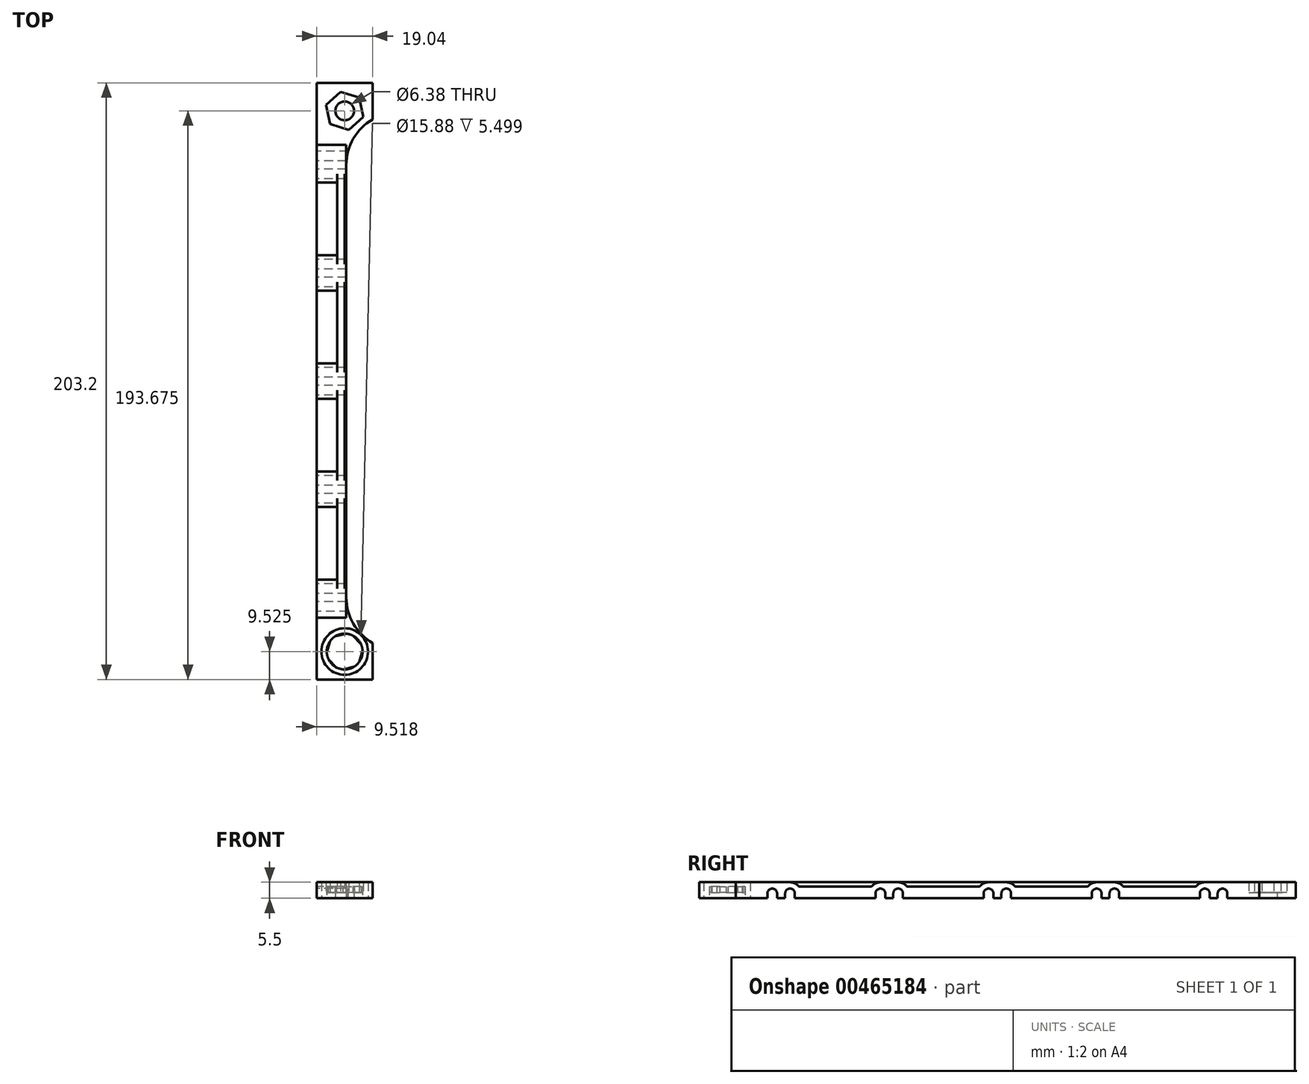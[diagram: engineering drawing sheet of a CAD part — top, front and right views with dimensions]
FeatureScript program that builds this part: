
annotation { "Feature Type Name" : "Feature", "Feature Type Description" : "" }
export const myFeature = defineFeature(function(context is Context, id is Id, definition is map)
    precondition{}
    {
        {
            var Q0;
            Q0=qCreatedBy(makeId("Top.planeOp"),FACE);
            var sketch = newSketch(context, id + "F0", { "sketchPlane" : qUnion([Q0])});
            skLineSegment(sketch, "E0.bottom", {"start": v(-101.58, -101.6) * mm, "end": v(-82.54, -101.6) * mm});
            skLineSegment(sketch, "E0.top", {"start": v(-101.58, 101.6) * mm, "end": v(-82.54, 101.6) * mm});
            skLineSegment(sketch, "E0.left", {"start": v(-101.58, -101.6) * mm, "end": v(-101.58, 101.6) * mm});
            skLineSegment(sketch, "E1.right", {"start": v(-92.06, -92.08) * mm, "end": v(-92.06, 92.08) * mm, "construction": true});
            skCircle(sketch, "E2.2.1.1", {"center": v(-73.66, -73.66) * mm, "radius": 17.85 * mm});
            skCircle(sketch, "E3.0.1.1", {"center": v(-73.66, -36.83) * mm, "radius": 17.85 * mm});
            skCircle(sketch, "E3.0.2.1", {"center": v(-73.66, 0) * mm, "radius": 17.85 * mm});
            skCircle(sketch, "E3.0.3.1", {"center": v(-73.66, 36.83) * mm, "radius": 17.85 * mm});
            skCircle(sketch, "E3.0.4.1", {"center": v(-73.66, 73.66) * mm, "radius": 17.85 * mm});
            skLineSegment(sketch, "E4.left", {"start": v(-94.6, 94.61) * mm, "end": v(-94.6, -94.62) * mm, "construction": true});
            skCircle(sketch, "E5", {"center": v(-92.06, 92.07) * mm, "radius": 6.1 * mm});
            skCircle(sketch, "E6", {"center": v(-92.06, 92.07) * mm, "radius": 3.19 * mm});
            skCircle(sketch, "E7.MirrorC", {"center": v(-92.06, -92.07) * mm, "radius": 3.19 * mm});
            skCircle(sketch, "E8.MirrorC", {"center": v(-92.06, -92.07) * mm, "radius": 6.1 * mm});
            skCircle(sketch, "E9", {"center": v(-92.06, 92.07) * mm, "radius": 7.94 * mm});
            skCircle(sketch, "E10.MirrorC", {"center": v(-92.06, -92.07) * mm, "radius": 7.94 * mm});
            skCircle(sketch, "E11", {"center": v(-73.65, -73.66) * mm, "radius": 16.38 * mm});
            skCircle(sketch, "E12.0.1.0", {"center": v(-73.65, -36.83) * mm, "radius": 16.38 * mm});
            skCircle(sketch, "E12.0.2.0", {"center": v(-73.65, 0) * mm, "radius": 16.38 * mm});
            skCircle(sketch, "E12.0.3.0", {"center": v(-73.65, 36.83) * mm, "radius": 16.38 * mm});
            skCircle(sketch, "E12.0.4.0", {"center": v(-73.65, 73.66) * mm, "radius": 16.38 * mm});
            skLineSegment(sketch, "E13.right", {"start": v(-101.58, -81.01) * mm, "end": v(-101.58, -68.33) * mm});
            skLineSegment(sketch, "E14.0.1.2", {"start": v(-101.6, -6.34) * mm, "end": v(-101.6, 6.34) * mm});
            skLineSegment(sketch, "E14.0.2.2", {"start": v(-101.62, 68.33) * mm, "end": v(-101.62, 81.01) * mm});
            skLineSegment(sketch, "E14.direction2", {"start": v(-101.58, -81.01) * mm, "end": v(-101.6, -6.34) * mm, "construction": true});
            skLineSegment(sketch, "E15", {"start": v(-101.58, 0) * mm, "end": v(-73.65, 0) * mm, "construction": true});
            skLineSegment(sketch, "E16", {"start": v(-82.54, 101.6) * mm, "end": v(-82.54, -101.6) * mm});
            skLineSegment(sketch, "E17", {"start": v(-92.06, -92.08) * mm, "end": v(-92.06, -101.6) * mm});
            skLineSegment(sketch, "E18", {"start": v(-73.65, 73.66) * mm, "end": v(-101.62, 73.66) * mm, "construction": true});
            skLineSegment(sketch, "E19", {"start": v(-73.65, 36.83) * mm, "end": v(-101.58, 36.83) * mm, "construction": true});
            skLineSegment(sketch, "E20", {"start": v(-73.65, -36.83) * mm, "end": v(-101.58, -36.83) * mm, "construction": true});
            skLineSegment(sketch, "E21", {"start": v(-73.65, -73.66) * mm, "end": v(-101.58, -73.66) * mm, "construction": true});
            skLineSegment(sketch, "E22", {"start": v(-91.5, 73.66) * mm, "end": v(-91.5, -73.66) * mm});
            skLineSegment(sketch, "E23.bottom", {"start": v(-94.6, -73.66) * mm, "end": v(-92.06, -73.66) * mm});
            skLineSegment(sketch, "E23.top", {"start": v(-94.6, 73.66) * mm, "end": v(-92.06, 73.66) * mm});
            skLineSegment(sketch, "E23.left", {"start": v(-94.6, -73.66) * mm, "end": v(-94.6, 73.66) * mm});
            skLineSegment(sketch, "E23.right", {"start": v(-92.06, -73.66) * mm, "end": v(-92.06, 73.66) * mm});
            skSolve(sketch);
        }
        {
            var Q0;
            {var subQ9=sQuery(id+"F0.wireOp",EDGE,"E0.top");Q0=makeQuery(id+"F0.imprint","IMPRINT",FACE,{"disambiguationData":[TD([[makeQuery(id+"F0.imprint","IMPRINT",EDGE,{"derivedFrom":subQ9}),-1.0]])]});}
            var Q1;
            Q1=makeQuery(id+"F0.imprint","IMPRINT",FACE,{"disambiguationData":[TD([[makeQuery(id+"F0.imprint","IMPRINT",EDGE,{"derivedFrom":sQuery(id+"F0.wireOp",EDGE,"E5")}),-1.0]])]});
            var Q2;
            Q2=makeQuery(id+"F0.imprint","IMPRINT",FACE,{"disambiguationData":[TD([[makeQuery(id+"F0.imprint","IMPRINT",EDGE,{"derivedFrom":sQuery(id+"F0.wireOp",EDGE,"E5")}),1.0]])]});
            var Q3;
            Q3=makeQuery(id+"F0.imprint","IMPRINT",FACE,{"disambiguationData":[TD([[makeQuery(id+"F0.imprint","IMPRINT",EDGE,{"derivedFrom":sQuery(id+"F0.wireOp",EDGE,"E8.MirrorC")}),1.0]])]});
            var Q4;
            Q4=makeQuery(id+"F0.imprint","IMPRINT",FACE,{"disambiguationData":[TD([[makeQuery(id+"F0.imprint","IMPRINT",EDGE,{"derivedFrom":sQuery(id+"F0.wireOp",EDGE,"E7.MirrorC")}),1.0]])]});
            extrude(context, id + "F1", {"entities" : qUnion([Q0, Q1, Q2, Q3, Q4]), "depth" : 4 * mm, "offsetDistance" : 25.4 * mm});
        }
        {
            var Q0;
            Q0=makeQuery(id+"F1.opExtrude","SWEPT_FACE",FACE,{"disambiguationData":[OSD([sQuery(id+"F0.wireOp",EDGE,"E0.left"),sQuery(id+"F0.wireOp",EDGE,"E13.right")])]});
            cPlane(context, id + "F2", {"entities" : qUnion([Q0]), "cplaneType" : CPlaneType.OFFSET, "offset" : 0 * mm, "width" : 152.4 * mm, "height" : 152.4 * mm});
        }
        {
            var Q0;
            Q0=qCreatedBy(id+"F2.planeOp",FACE);
            var sketch = newSketch(context, id + "F3", { "sketchPlane" : qUnion([Q0])});
            skLineSegment(sketch, "E24.bottom", {"start": v(-75.03, 0) * mm, "end": v(-78.33, 0) * mm});
            skLineSegment(sketch, "E24.top", {"start": v(-75.03, 1.65) * mm, "end": v(-78.33, 1.65) * mm});
            skLineSegment(sketch, "E24.left", {"start": v(-75.03, 0) * mm, "end": v(-75.03, 1.65) * mm});
            skLineSegment(sketch, "E24.right", {"start": v(-78.33, 0) * mm, "end": v(-78.33, 1.65) * mm});
            skLineSegment(sketch, "E25.bottom", {"start": v(-72.29, 0) * mm, "end": v(-68.99, 0) * mm});
            skLineSegment(sketch, "E25.top", {"start": v(-72.29, 1.65) * mm, "end": v(-68.99, 1.65) * mm});
            skLineSegment(sketch, "E25.left", {"start": v(-72.29, 0) * mm, "end": v(-72.29, 1.65) * mm});
            skLineSegment(sketch, "E25.right", {"start": v(-68.99, 0) * mm, "end": v(-68.99, 1.65) * mm});
            skArc(sketch, "E26", {"start": v(-75.03, 1.65) * mm, "mid": v(-76.68, 3.3) * mm, "end": v(-78.33, 1.65) * mm});
            skArc(sketch, "E27", {"start": v(-68.99, 1.65) * mm, "mid": v(-70.64, 3.3) * mm, "end": v(-72.29, 1.65) * mm});
            skArc(sketch, "E28", {"start": v(-70.64, 5.46) * mm, "mid": v(-67.94, 4.34) * mm, "end": v(-66.83, 1.65) * mm});
            skPoint(sketch, "E28.startSnap0", {"position": v(-70.64, 3.3) * mm});
            skLineSegment(sketch, "E29", {"start": v(-76.68, 5.46) * mm, "end": v(-70.64, 5.46) * mm});
            skLineSegment(sketch, "E30", {"start": v(-80.5, 1.65) * mm, "end": v(-78.33, 1.65) * mm});
            skLineSegment(sketch, "E31", {"start": v(-75.03, 1.65) * mm, "end": v(-72.29, 1.65) * mm});
            skLineSegment(sketch, "E32", {"start": v(-68.99, 1.65) * mm, "end": v(-66.83, 1.65) * mm});
            skLineSegment(sketch, "E33", {"start": v(-76.68, 1.65) * mm, "end": v(-76.68, 0) * mm, "construction": true});
            skLineSegment(sketch, "E34", {"start": v(-70.64, 1.65) * mm, "end": v(-70.64, 0) * mm, "construction": true});
            skLineSegment(sketch, "E35.bottom", {"start": v(-38.2, 0) * mm, "end": v(-41.5, 0) * mm});
            skLineSegment(sketch, "E35.top", {"start": v(-38.2, 1.65) * mm, "end": v(-41.5, 1.65) * mm});
            skLineSegment(sketch, "E35.left", {"start": v(-38.2, 0) * mm, "end": v(-38.2, 1.65) * mm});
            skLineSegment(sketch, "E35.right", {"start": v(-41.5, 0) * mm, "end": v(-41.5, 1.65) * mm});
            skLineSegment(sketch, "E36.bottom", {"start": v(-35.46, 0) * mm, "end": v(-32.16, 0) * mm});
            skLineSegment(sketch, "E36.top", {"start": v(-35.46, 1.65) * mm, "end": v(-32.16, 1.65) * mm});
            skLineSegment(sketch, "E36.left", {"start": v(-35.46, 0) * mm, "end": v(-35.46, 1.65) * mm});
            skLineSegment(sketch, "E36.right", {"start": v(-32.16, 0) * mm, "end": v(-32.16, 1.65) * mm});
            skArc(sketch, "E37", {"start": v(-38.2, 1.65) * mm, "mid": v(-39.85, 3.3) * mm, "end": v(-41.5, 1.65) * mm});
            skArc(sketch, "E38", {"start": v(-32.16, 1.65) * mm, "mid": v(-33.8, 3.3) * mm, "end": v(-35.46, 1.65) * mm});
            skArc(sketch, "E39", {"start": v(-43.66, 1.65) * mm, "mid": v(-42.55, 4.34) * mm, "end": v(-39.85, 5.46) * mm});
            skArc(sketch, "E40", {"start": v(-33.8, 5.46) * mm, "mid": v(-31.11, 4.34) * mm, "end": v(-30, 1.65) * mm});
            skPoint(sketch, "E40.startSnap0", {"position": v(-33.8, 3.3) * mm});
            skLineSegment(sketch, "E41", {"start": v(-39.85, 5.46) * mm, "end": v(-33.8, 5.46) * mm});
            skLineSegment(sketch, "E42", {"start": v(-43.66, 1.65) * mm, "end": v(-41.5, 1.65) * mm});
            skLineSegment(sketch, "E43", {"start": v(-38.2, 1.65) * mm, "end": v(-35.46, 1.65) * mm});
            skLineSegment(sketch, "E44", {"start": v(-32.16, 1.65) * mm, "end": v(-30, 1.65) * mm});
            skLineSegment(sketch, "E45", {"start": v(-39.85, 1.65) * mm, "end": v(-39.85, 0) * mm, "construction": true});
            skLineSegment(sketch, "E46", {"start": v(-33.8, 1.65) * mm, "end": v(-33.8, 0) * mm, "construction": true});
            skLineSegment(sketch, "E47.bottom", {"start": v(-1.37, 0) * mm, "end": v(-4.67, 0) * mm});
            skLineSegment(sketch, "E47.top", {"start": v(-1.37, 1.65) * mm, "end": v(-4.67, 1.65) * mm});
            skLineSegment(sketch, "E47.left", {"start": v(-1.37, 0) * mm, "end": v(-1.37, 1.65) * mm});
            skLineSegment(sketch, "E47.right", {"start": v(-4.67, 0) * mm, "end": v(-4.67, 1.65) * mm});
            skLineSegment(sketch, "E48.bottom", {"start": v(1.37, 0) * mm, "end": v(4.67, 0) * mm});
            skLineSegment(sketch, "E48.top", {"start": v(1.37, 1.65) * mm, "end": v(4.67, 1.65) * mm});
            skLineSegment(sketch, "E48.left", {"start": v(1.37, 0) * mm, "end": v(1.37, 1.65) * mm});
            skLineSegment(sketch, "E48.right", {"start": v(4.67, 0) * mm, "end": v(4.67, 1.65) * mm});
            skArc(sketch, "E49", {"start": v(-1.37, 1.65) * mm, "mid": v(-3.02, 3.3) * mm, "end": v(-4.67, 1.65) * mm});
            skArc(sketch, "E50", {"start": v(4.67, 1.65) * mm, "mid": v(3.02, 3.3) * mm, "end": v(1.37, 1.65) * mm});
            skArc(sketch, "E51", {"start": v(-6.83, 1.65) * mm, "mid": v(-5.72, 4.34) * mm, "end": v(-3.02, 5.46) * mm});
            skArc(sketch, "E52", {"start": v(3.02, 5.46) * mm, "mid": v(5.72, 4.34) * mm, "end": v(6.83, 1.65) * mm});
            skPoint(sketch, "E52.startSnap0", {"position": v(3.02, 3.3) * mm});
            skLineSegment(sketch, "E53", {"start": v(-3.02, 5.46) * mm, "end": v(3.02, 5.46) * mm});
            skLineSegment(sketch, "E54", {"start": v(-6.83, 1.65) * mm, "end": v(-4.67, 1.65) * mm});
            skLineSegment(sketch, "E55", {"start": v(-1.37, 1.65) * mm, "end": v(1.37, 1.65) * mm});
            skLineSegment(sketch, "E56", {"start": v(4.67, 1.65) * mm, "end": v(6.83, 1.65) * mm});
            skLineSegment(sketch, "E57", {"start": v(-3.02, 1.65) * mm, "end": v(-3.02, 0) * mm, "construction": true});
            skLineSegment(sketch, "E58", {"start": v(3.02, 1.65) * mm, "end": v(3.02, 0) * mm, "construction": true});
            skLineSegment(sketch, "E59.bottom", {"start": v(35.46, 0) * mm, "end": v(32.16, 0) * mm});
            skLineSegment(sketch, "E59.top", {"start": v(35.46, 1.65) * mm, "end": v(32.16, 1.65) * mm});
            skLineSegment(sketch, "E59.left", {"start": v(35.46, 0) * mm, "end": v(35.46, 1.65) * mm});
            skLineSegment(sketch, "E59.right", {"start": v(32.16, 0) * mm, "end": v(32.16, 1.65) * mm});
            skLineSegment(sketch, "E60.bottom", {"start": v(38.2, 0) * mm, "end": v(41.5, 0) * mm});
            skLineSegment(sketch, "E60.top", {"start": v(38.2, 1.65) * mm, "end": v(41.5, 1.65) * mm});
            skLineSegment(sketch, "E60.left", {"start": v(38.2, 0) * mm, "end": v(38.2, 1.65) * mm});
            skLineSegment(sketch, "E60.right", {"start": v(41.5, 0) * mm, "end": v(41.5, 1.65) * mm});
            skArc(sketch, "E61", {"start": v(35.46, 1.65) * mm, "mid": v(33.8, 3.3) * mm, "end": v(32.16, 1.65) * mm});
            skArc(sketch, "E62", {"start": v(41.5, 1.65) * mm, "mid": v(39.85, 3.3) * mm, "end": v(38.2, 1.65) * mm});
            skArc(sketch, "E63", {"start": v(30, 1.65) * mm, "mid": v(31.11, 4.34) * mm, "end": v(33.8, 5.46) * mm});
            skArc(sketch, "E64", {"start": v(39.85, 5.46) * mm, "mid": v(42.55, 4.34) * mm, "end": v(43.66, 1.65) * mm});
            skPoint(sketch, "E64.startSnap0", {"position": v(39.85, 3.3) * mm});
            skLineSegment(sketch, "E65", {"start": v(33.8, 5.46) * mm, "end": v(39.85, 5.46) * mm});
            skLineSegment(sketch, "E66", {"start": v(30, 1.65) * mm, "end": v(32.16, 1.65) * mm});
            skLineSegment(sketch, "E67", {"start": v(35.46, 1.65) * mm, "end": v(38.2, 1.65) * mm});
            skLineSegment(sketch, "E68", {"start": v(41.5, 1.65) * mm, "end": v(43.66, 1.65) * mm});
            skLineSegment(sketch, "E69", {"start": v(33.8, 1.65) * mm, "end": v(33.8, 0) * mm, "construction": true});
            skLineSegment(sketch, "E70", {"start": v(39.85, 1.65) * mm, "end": v(39.85, 0) * mm, "construction": true});
            skLineSegment(sketch, "E71.bottom", {"start": v(72.29, 0) * mm, "end": v(68.99, 0) * mm});
            skLineSegment(sketch, "E71.top", {"start": v(72.29, 1.65) * mm, "end": v(68.99, 1.65) * mm});
            skLineSegment(sketch, "E71.left", {"start": v(72.29, 0) * mm, "end": v(72.29, 1.65) * mm});
            skLineSegment(sketch, "E71.right", {"start": v(68.99, 0) * mm, "end": v(68.99, 1.65) * mm});
            skLineSegment(sketch, "E72.bottom", {"start": v(75.03, 0) * mm, "end": v(78.33, 0) * mm});
            skLineSegment(sketch, "E72.top", {"start": v(75.03, 1.65) * mm, "end": v(78.33, 1.65) * mm});
            skLineSegment(sketch, "E72.left", {"start": v(75.03, 0) * mm, "end": v(75.03, 1.65) * mm});
            skLineSegment(sketch, "E72.right", {"start": v(78.33, 0) * mm, "end": v(78.33, 1.65) * mm});
            skArc(sketch, "E73", {"start": v(72.29, 1.65) * mm, "mid": v(70.64, 3.3) * mm, "end": v(68.99, 1.65) * mm});
            skArc(sketch, "E74", {"start": v(78.33, 1.65) * mm, "mid": v(76.68, 3.3) * mm, "end": v(75.03, 1.65) * mm});
            skArc(sketch, "E75", {"start": v(66.83, 1.65) * mm, "mid": v(67.94, 4.34) * mm, "end": v(70.64, 5.46) * mm});
            skPoint(sketch, "E76.startSnap0", {"position": v(76.68, 3.3) * mm});
            skLineSegment(sketch, "E77", {"start": v(70.64, 5.46) * mm, "end": v(76.68, 5.46) * mm});
            skLineSegment(sketch, "E78", {"start": v(66.83, 1.65) * mm, "end": v(68.99, 1.65) * mm});
            skLineSegment(sketch, "E79", {"start": v(72.29, 1.65) * mm, "end": v(75.03, 1.65) * mm});
            skLineSegment(sketch, "E80", {"start": v(78.33, 1.65) * mm, "end": v(80.5, 1.65) * mm});
            skLineSegment(sketch, "E81", {"start": v(70.64, 1.65) * mm, "end": v(70.64, 0) * mm, "construction": true});
            skLineSegment(sketch, "E82", {"start": v(76.68, 1.65) * mm, "end": v(76.68, 0) * mm, "construction": true});
            skLineSegment(sketch, "E83", {"start": v(80.5, 1.65) * mm, "end": v(80.5, 5.46) * mm});
            skLineSegment(sketch, "E84", {"start": v(80.5, 5.46) * mm, "end": v(76.68, 5.46) * mm});
            skLineSegment(sketch, "E85", {"start": v(-80.5, 1.65) * mm, "end": v(-80.5, 5.46) * mm});
            skLineSegment(sketch, "E86", {"start": v(-80.5, 5.46) * mm, "end": v(-76.68, 5.46) * mm});
            skSolve(sketch);
        }
        {
            var Q0;
            Q0=makeQuery(id+"F0.imprint","IMPRINT",FACE,{"disambiguationData":[TD([[makeQuery(id+"F0.imprint","IMPRINT",EDGE,{"derivedFrom":sQuery(id+"F0.wireOp",EDGE,"E23.bottom")}),1.0]])]});
            extrude(context, id + "F4", {"entities" : qUnion([Q0]), "operationType" : NewBodyOperationType.ADD, "depth" : 5.46 * mm, "offsetDistance" : 25.4 * mm});
        }
        {
            var Q0;
            Q0=makeQuery(id+"F3.imprint","IMPRINT",FACE,{"disambiguationData":[TD([[makeQuery(id+"F3.imprint","IMPRINT",EDGE,{"derivedFrom":sQuery(id+"F3.wireOp",EDGE,"E26")}),-1.0]])]});
            var Q1;
            Q1=makeQuery(id+"F3.imprint","IMPRINT",FACE,{"disambiguationData":[TD([[makeQuery(id+"F3.imprint","IMPRINT",EDGE,{"derivedFrom":sQuery(id+"F3.wireOp",EDGE,"E37")}),-1.0]])]});
            var Q2;
            Q2=makeQuery(id+"F3.imprint","IMPRINT",FACE,{"disambiguationData":[TD([[makeQuery(id+"F3.imprint","IMPRINT",EDGE,{"derivedFrom":sQuery(id+"F3.wireOp",EDGE,"E49")}),-1.0]])]});
            var Q3;
            Q3=makeQuery(id+"F3.imprint","IMPRINT",FACE,{"disambiguationData":[TD([[makeQuery(id+"F3.imprint","IMPRINT",EDGE,{"derivedFrom":sQuery(id+"F3.wireOp",EDGE,"E61")}),-1.0]])]});
            var Q4;
            Q4=makeQuery(id+"F3.imprint","IMPRINT",FACE,{"disambiguationData":[TD([[makeQuery(id+"F3.imprint","IMPRINT",EDGE,{"derivedFrom":sQuery(id+"F3.wireOp",EDGE,"E73")}),-1.0]])]});
            var Q5;
            Q5=makeQuery(id+"F1.opExtrude","SWEPT_FACE",FACE,{"disambiguationData":[OSD([sQuery(id+"F0.wireOp",EDGE,"E22")])]});
            extrude(context, id + "F5", {"entities" : qUnion([Q0, Q1, Q2, Q3, Q4]), "operationType" : NewBodyOperationType.ADD, "endBound" : BoundingType.UP_TO_SURFACE, "oppositeDirection" : true, "depth" : 25.4 * mm, "endBoundEntityFace" : qUnion([Q5]), "offsetDistance" : 25.4 * mm});
        }
        {
            var Q0;
            Q0=makeQuery(id+"F3.imprint","IMPRINT",FACE,{"disambiguationData":[TD([[makeQuery(id+"F3.imprint","IMPRINT",EDGE,{"derivedFrom":sQuery(id+"F3.wireOp",EDGE,"E24.bottom")}),-1.0]])]});
            var Q1;
            Q1=makeQuery(id+"F3.imprint","IMPRINT",FACE,{"disambiguationData":[TD([[makeQuery(id+"F3.imprint","IMPRINT",EDGE,{"derivedFrom":sQuery(id+"F3.wireOp",EDGE,"E25.bottom")}),1.0]])]});
            var Q2;
            Q2=makeQuery(id+"F3.imprint","IMPRINT",FACE,{"disambiguationData":[TD([[makeQuery(id+"F3.imprint","IMPRINT",EDGE,{"derivedFrom":sQuery(id+"F3.wireOp",EDGE,"E25.top")}),1.0]])]});
            var Q3;
            Q3=makeQuery(id+"F3.imprint","IMPRINT",FACE,{"disambiguationData":[TD([[makeQuery(id+"F3.imprint","IMPRINT",EDGE,{"derivedFrom":sQuery(id+"F3.wireOp",EDGE,"E24.top")}),-1.0]])]});
            var Q4;
            Q4=makeQuery(id+"F3.imprint","IMPRINT",FACE,{"disambiguationData":[TD([[makeQuery(id+"F3.imprint","IMPRINT",EDGE,{"derivedFrom":sQuery(id+"F3.wireOp",EDGE,"E35.top")}),-1.0]])]});
            var Q5;
            Q5=makeQuery(id+"F3.imprint","IMPRINT",FACE,{"disambiguationData":[TD([[makeQuery(id+"F3.imprint","IMPRINT",EDGE,{"derivedFrom":sQuery(id+"F3.wireOp",EDGE,"E36.top")}),1.0]])]});
            var Q6;
            Q6=makeQuery(id+"F3.imprint","IMPRINT",FACE,{"disambiguationData":[TD([[makeQuery(id+"F3.imprint","IMPRINT",EDGE,{"derivedFrom":sQuery(id+"F3.wireOp",EDGE,"E36.bottom")}),1.0]])]});
            var Q7;
            Q7=makeQuery(id+"F3.imprint","IMPRINT",FACE,{"disambiguationData":[TD([[makeQuery(id+"F3.imprint","IMPRINT",EDGE,{"derivedFrom":sQuery(id+"F3.wireOp",EDGE,"E35.bottom")}),-1.0]])]});
            var Q8;
            Q8=makeQuery(id+"F3.imprint","IMPRINT",FACE,{"disambiguationData":[TD([[makeQuery(id+"F3.imprint","IMPRINT",EDGE,{"derivedFrom":sQuery(id+"F3.wireOp",EDGE,"E47.top")}),-1.0]])]});
            var Q9;
            Q9=makeQuery(id+"F3.imprint","IMPRINT",FACE,{"disambiguationData":[TD([[makeQuery(id+"F3.imprint","IMPRINT",EDGE,{"derivedFrom":sQuery(id+"F3.wireOp",EDGE,"E47.bottom")}),-1.0]])]});
            var Q10;
            Q10=makeQuery(id+"F3.imprint","IMPRINT",FACE,{"disambiguationData":[TD([[makeQuery(id+"F3.imprint","IMPRINT",EDGE,{"derivedFrom":sQuery(id+"F3.wireOp",EDGE,"E48.top")}),1.0]])]});
            var Q11;
            Q11=makeQuery(id+"F3.imprint","IMPRINT",FACE,{"disambiguationData":[TD([[makeQuery(id+"F3.imprint","IMPRINT",EDGE,{"derivedFrom":sQuery(id+"F3.wireOp",EDGE,"E48.bottom")}),1.0]])]});
            var Q12;
            Q12=makeQuery(id+"F3.imprint","IMPRINT",FACE,{"disambiguationData":[TD([[makeQuery(id+"F3.imprint","IMPRINT",EDGE,{"derivedFrom":sQuery(id+"F3.wireOp",EDGE,"E59.bottom")}),-1.0]])]});
            var Q13;
            Q13=makeQuery(id+"F3.imprint","IMPRINT",FACE,{"disambiguationData":[TD([[makeQuery(id+"F3.imprint","IMPRINT",EDGE,{"derivedFrom":sQuery(id+"F3.wireOp",EDGE,"E59.top")}),-1.0]])]});
            var Q14;
            Q14=makeQuery(id+"F3.imprint","IMPRINT",FACE,{"disambiguationData":[TD([[makeQuery(id+"F3.imprint","IMPRINT",EDGE,{"derivedFrom":sQuery(id+"F3.wireOp",EDGE,"E60.bottom")}),1.0]])]});
            var Q15;
            Q15=makeQuery(id+"F3.imprint","IMPRINT",FACE,{"disambiguationData":[TD([[makeQuery(id+"F3.imprint","IMPRINT",EDGE,{"derivedFrom":sQuery(id+"F3.wireOp",EDGE,"E60.top")}),1.0]])]});
            var Q16;
            Q16=makeQuery(id+"F3.imprint","IMPRINT",FACE,{"disambiguationData":[TD([[makeQuery(id+"F3.imprint","IMPRINT",EDGE,{"derivedFrom":sQuery(id+"F3.wireOp",EDGE,"E71.bottom")}),-1.0]])]});
            var Q17;
            Q17=makeQuery(id+"F3.imprint","IMPRINT",FACE,{"disambiguationData":[TD([[makeQuery(id+"F3.imprint","IMPRINT",EDGE,{"derivedFrom":sQuery(id+"F3.wireOp",EDGE,"E71.top")}),-1.0]])]});
            var Q18;
            Q18=makeQuery(id+"F3.imprint","IMPRINT",FACE,{"disambiguationData":[TD([[makeQuery(id+"F3.imprint","IMPRINT",EDGE,{"derivedFrom":sQuery(id+"F3.wireOp",EDGE,"E72.top")}),1.0]])]});
            var Q19;
            Q19=makeQuery(id+"F3.imprint","IMPRINT",FACE,{"disambiguationData":[TD([[makeQuery(id+"F3.imprint","IMPRINT",EDGE,{"derivedFrom":sQuery(id+"F3.wireOp",EDGE,"E72.bottom")}),1.0]])]});
            var Q20;
            Q20=makeQuery(id+"F1.opExtrude","SWEPT_BODY",BODY,{"disambiguationData":[OSD([sQuery(id+"F0.wireOp",EDGE,"E0.bottom"),sQuery(id+"F0.wireOp",EDGE,"E0.top"),sQuery(id+"F0.wireOp",EDGE,"E0.left"),sQuery(id+"F0.wireOp",EDGE,"E2.2.1.1"),sQuery(id+"F0.wireOp",EDGE,"E3.0.4.1"),sQuery(id+"F0.wireOp",EDGE,"E6"),sQuery(id+"F0.wireOp",EDGE,"E7.MirrorC"),sQuery(id+"F0.wireOp",EDGE,"E13.right"),sQuery(id+"F0.wireOp",EDGE,"E16"),sQuery(id+"F0.wireOp",EDGE,"E22")])]});
            extrude(context, id + "F6", {"entities" : qUnion([Q0, Q1, Q2, Q3, Q4, Q5, Q6, Q7, Q8, Q9, Q10, Q11, Q12, Q13, Q14, Q15, Q16, Q17, Q18, Q19]), "operationType" : NewBodyOperationType.REMOVE, "endBound" : BoundingType.THROUGH_ALL, "oppositeDirection" : true, "depth" : 25.4 * mm, "endBoundEntityBody" : qUnion([Q20]), "offsetDistance" : 25.4 * mm});
        }
        {
            var Q0;
            {var subQ0=sQuery(id+"F0.wireOp",EDGE,"E13.right");var subQ1=sQuery(id+"F0.wireOp",EDGE,"E0.left");var subQ2=sQuery(id+"F3.wireOp",EDGE,"f0gCdHVo-Gz2e-MZJZ-KHlR-wAMuaOjWp0eY");var subQ3=sQuery(id+"F0.wireOp",EDGE,"E22");var subQ4=sQuery(id+"F0.wireOp",EDGE,"E16");var subQ5=sQuery(id+"F0.wireOp",EDGE,"E0.top");var subQ6=sQuery(id+"F0.wireOp",EDGE,"E3.0.4.1");var subQ7=sQuery(id+"F0.wireOp",EDGE,"E6");Q0=makeQuery(id+"F5.boolean.opBoolean","SPLIT",FACE,{"disambiguationData":[TD([makeQuery(id+"F1.opExtrude","SWEPT_FACE",FACE,{"disambiguationData":[OSD([subQ5])]}),makeQuery(id+"F1.opExtrude","SWEPT_FACE",FACE,{"disambiguationData":[OSD([subQ1,subQ0])]}),makeQuery(id+"F1.opExtrude","SWEPT_FACE",FACE,{"disambiguationData":[OSD([subQ6])]}),makeQuery(id+"F1.opExtrude","SWEPT_FACE",FACE,{"disambiguationData":[OSD([subQ7])]}),makeQuery(id+"F1.opExtrude","SWEPT_FACE",FACE,{"disambiguationData":[OSD([subQ4]),TDD([makeQuery(id+"F0.imprint","IMPRINT",EDGE,{"disambiguationData":[TD([[makeQuery(id+"F0.imprint","INTERSECT",VERTEX,{"derivedFrom":[subQ5,subQ4]}),-1.0]])],"derivedFrom":subQ4})])]}),makeQuery(id+"F1.opExtrude","SWEPT_FACE",FACE,{"disambiguationData":[OSD([subQ3])]}),makeQuery(id+"F5.opExtrude","CAP_FACE",FACE,{"disambiguationData":[OSD([sQuery(id+"F3.wireOp",EDGE,"E26"),sQuery(id+"F3.wireOp",EDGE,"E27"),subQ2,sQuery(id+"F3.wireOp",EDGE,"E28"),sQuery(id+"F3.wireOp",EDGE,"E29"),sQuery(id+"F3.wireOp",EDGE,"E30"),sQuery(id+"F3.wireOp",EDGE,"E31"),sQuery(id+"F3.wireOp",EDGE,"E32")])],"isStart":true}),makeQuery(id+"F5.opExtrude","SWEPT_FACE",FACE,{"disambiguationData":[OSD([subQ2])]}),makeQuery(id+"F5.opExtrude","CAP_FACE",FACE,{"disambiguationData":[OSD([sQuery(id+"F3.wireOp",EDGE,"E37"),sQuery(id+"F3.wireOp",EDGE,"E38"),sQuery(id+"F3.wireOp",EDGE,"E39"),sQuery(id+"F3.wireOp",EDGE,"E40"),sQuery(id+"F3.wireOp",EDGE,"E41"),sQuery(id+"F3.wireOp",EDGE,"E42"),sQuery(id+"F3.wireOp",EDGE,"E43"),sQuery(id+"F3.wireOp",EDGE,"E44")])],"isStart":true}),makeQuery(id+"F5.opExtrude","CAP_FACE",FACE,{"disambiguationData":[OSD([sQuery(id+"F3.wireOp",EDGE,"E49"),sQuery(id+"F3.wireOp",EDGE,"E50"),sQuery(id+"F3.wireOp",EDGE,"E51"),sQuery(id+"F3.wireOp",EDGE,"E52"),sQuery(id+"F3.wireOp",EDGE,"E53"),sQuery(id+"F3.wireOp",EDGE,"E54"),sQuery(id+"F3.wireOp",EDGE,"E55"),sQuery(id+"F3.wireOp",EDGE,"E56")])],"isStart":true}),makeQuery(id+"F5.opExtrude","CAP_FACE",FACE,{"disambiguationData":[OSD([sQuery(id+"F3.wireOp",EDGE,"E61"),sQuery(id+"F3.wireOp",EDGE,"E62"),sQuery(id+"F3.wireOp",EDGE,"E63"),sQuery(id+"F3.wireOp",EDGE,"E64"),sQuery(id+"F3.wireOp",EDGE,"E65"),sQuery(id+"F3.wireOp",EDGE,"E66"),sQuery(id+"F3.wireOp",EDGE,"E67"),sQuery(id+"F3.wireOp",EDGE,"E68")])],"isStart":true}),makeQuery(id+"F5.opExtrude","CAP_FACE",FACE,{"disambiguationData":[OSD([sQuery(id+"F3.wireOp",EDGE,"E73"),sQuery(id+"F3.wireOp",EDGE,"E74"),sQuery(id+"F3.wireOp",EDGE,"E75"),sQuery(id+"F3.wireOp",EDGE,"E76"),sQuery(id+"F3.wireOp",EDGE,"E77"),sQuery(id+"F3.wireOp",EDGE,"E78"),sQuery(id+"F3.wireOp",EDGE,"E79"),sQuery(id+"F3.wireOp",EDGE,"E80")])],"isStart":true}),makeQuery(id+"F5.opExtrude","CAP_FACE",FACE,{"disambiguationData":[OSD([subQ3]),OD(0.0)],"isStart":false}),makeQuery(id+"F5.opExtrude","CAP_FACE",FACE,{"disambiguationData":[OSD([subQ3]),OD(1.0)],"isStart":false}),makeQuery(id+"F5.opExtrude","CAP_FACE",FACE,{"disambiguationData":[OSD([subQ3]),OD(2.0)],"isStart":false}),makeQuery(id+"F5.opExtrude","CAP_FACE",FACE,{"disambiguationData":[OSD([subQ3]),OD(3.0)],"isStart":false}),makeQuery(id+"F5.opExtrude","CAP_FACE",FACE,{"disambiguationData":[OSD([subQ3]),OD(4.0)],"isStart":false})])],"derivedFrom":makeQuery(id+"F1.opExtrude","CAP_FACE",FACE,{"disambiguationData":[OSD([sQuery(id+"F0.wireOp",EDGE,"E0.bottom"),subQ5,subQ1,sQuery(id+"F0.wireOp",EDGE,"E2.2.1.1"),subQ6,subQ7,sQuery(id+"F0.wireOp",EDGE,"E7.MirrorC"),subQ0,subQ4,subQ3,sQuery(id+"F0.wireOp",EDGE,"E23.bottom"),sQuery(id+"F0.wireOp",EDGE,"E23.top"),sQuery(id+"F0.wireOp",EDGE,"E23.left"),sQuery(id+"F0.wireOp",EDGE,"E23.right")])],"isStart":false})});}
            cPlane(context, id + "F7", {"entities" : qUnion([Q0]), "cplaneType" : CPlaneType.OFFSET, "offset" : 2 * mm, "oppositeDirection" : true, "width" : 152.4 * mm, "height" : 152.4 * mm});
        }
        {
            var Q0;
            Q0=qCreatedBy(id+"F7.planeOp",FACE);
            var sketch = newSketch(context, id + "F8", { "sketchPlane" : qUnion([Q0])});
            skCircle(sketch, "E87.cCircle", {"center": v(-92.06, 92.08) * mm, "radius": 5.75 * mm, "construction": true});
            skLineSegment(sketch, "E87.0", {"start": v(-85.73, 90.06) * mm, "end": v(-90.64, 85.59) * mm});
            skLineSegment(sketch, "E87.1", {"start": v(-90.64, 85.59) * mm, "end": v(-96.97, 87.6) * mm});
            skLineSegment(sketch, "E87.2", {"start": v(-96.97, 87.6) * mm, "end": v(-98.4, 94.1) * mm});
            skLineSegment(sketch, "E87.3", {"start": v(-98.4, 94.1) * mm, "end": v(-93.48, 98.57) * mm});
            skLineSegment(sketch, "E87.4", {"start": v(-93.48, 98.57) * mm, "end": v(-87.15, 96.56) * mm});
            skLineSegment(sketch, "E87.5", {"start": v(-87.15, 96.56) * mm, "end": v(-85.73, 90.06) * mm});
            skPoint(sketch, "E87.0.midPoint", {"position": v(-88.19, 87.83) * mm});
            skCircle(sketch, "E88.cCircle", {"center": v(-92.06, -92.07) * mm, "radius": 5.75 * mm, "construction": true});
            skLineSegment(sketch, "E88.0", {"start": v(-85.6, -90.5) * mm, "end": v(-87.47, -96.88) * mm});
            skLineSegment(sketch, "E88.1", {"start": v(-87.47, -96.88) * mm, "end": v(-93.92, -98.45) * mm});
            skLineSegment(sketch, "E88.2", {"start": v(-93.92, -98.45) * mm, "end": v(-98.52, -93.65) * mm});
            skLineSegment(sketch, "E88.3", {"start": v(-98.52, -93.65) * mm, "end": v(-96.66, -87.27) * mm});
            skLineSegment(sketch, "E88.4", {"start": v(-96.66, -87.27) * mm, "end": v(-90.2, -85.7) * mm});
            skLineSegment(sketch, "E88.5", {"start": v(-90.2, -85.7) * mm, "end": v(-85.6, -90.5) * mm});
            skPoint(sketch, "E88.0.midPoint", {"position": v(-86.54, -93.69) * mm});
            skSolve(sketch);
        }
        {
            var Q0;
            {var subQ0=sQuery(id+"F0.wireOp",EDGE,"E22");var subQ1=sQuery(id+"F0.wireOp",EDGE,"E13.right");var subQ2=sQuery(id+"F0.wireOp",EDGE,"E0.left");var subQ3=sQuery(id+"F0.wireOp",EDGE,"E16");var subQ4=sQuery(id+"F0.wireOp",EDGE,"E0.bottom");var subQ5=sQuery(id+"F0.wireOp",EDGE,"E2.2.1.1");var subQ6=sQuery(id+"F0.wireOp",EDGE,"E7.MirrorC");var subQ7=sQuery(id+"F3.wireOp",EDGE,"E76");Q0=makeQuery(id+"F5.boolean.opBoolean","SPLIT",FACE,{"disambiguationData":[TD([makeQuery(id+"F1.opExtrude","SWEPT_FACE",FACE,{"disambiguationData":[OSD([subQ4])]}),makeQuery(id+"F1.opExtrude","SWEPT_FACE",FACE,{"disambiguationData":[OSD([subQ2,subQ1])]}),makeQuery(id+"F1.opExtrude","SWEPT_FACE",FACE,{"disambiguationData":[OSD([subQ5])]}),makeQuery(id+"F1.opExtrude","SWEPT_FACE",FACE,{"disambiguationData":[OSD([subQ6])]}),makeQuery(id+"F1.opExtrude","SWEPT_FACE",FACE,{"disambiguationData":[OSD([subQ3]),TDD([makeQuery(id+"F0.imprint","IMPRINT",EDGE,{"disambiguationData":[TD([[makeQuery(id+"F0.imprint","INTERSECT",VERTEX,{"derivedFrom":[subQ4,subQ3]}),1.0]])],"derivedFrom":subQ3})])]}),makeQuery(id+"F1.opExtrude","SWEPT_FACE",FACE,{"disambiguationData":[OSD([subQ0])]}),makeQuery(id+"F5.opExtrude","CAP_FACE",FACE,{"disambiguationData":[OSD([sQuery(id+"F3.wireOp",EDGE,"E26"),sQuery(id+"F3.wireOp",EDGE,"E27"),sQuery(id+"F3.wireOp",EDGE,"f0gCdHVo-Gz2e-MZJZ-KHlR-wAMuaOjWp0eY"),sQuery(id+"F3.wireOp",EDGE,"E28"),sQuery(id+"F3.wireOp",EDGE,"E29"),sQuery(id+"F3.wireOp",EDGE,"E30"),sQuery(id+"F3.wireOp",EDGE,"E31"),sQuery(id+"F3.wireOp",EDGE,"E32")])],"isStart":true}),makeQuery(id+"F5.opExtrude","CAP_FACE",FACE,{"disambiguationData":[OSD([sQuery(id+"F3.wireOp",EDGE,"E37"),sQuery(id+"F3.wireOp",EDGE,"E38"),sQuery(id+"F3.wireOp",EDGE,"E39"),sQuery(id+"F3.wireOp",EDGE,"E40"),sQuery(id+"F3.wireOp",EDGE,"E41"),sQuery(id+"F3.wireOp",EDGE,"E42"),sQuery(id+"F3.wireOp",EDGE,"E43"),sQuery(id+"F3.wireOp",EDGE,"E44")])],"isStart":true}),makeQuery(id+"F5.opExtrude","CAP_FACE",FACE,{"disambiguationData":[OSD([sQuery(id+"F3.wireOp",EDGE,"E49"),sQuery(id+"F3.wireOp",EDGE,"E50"),sQuery(id+"F3.wireOp",EDGE,"E51"),sQuery(id+"F3.wireOp",EDGE,"E52"),sQuery(id+"F3.wireOp",EDGE,"E53"),sQuery(id+"F3.wireOp",EDGE,"E54"),sQuery(id+"F3.wireOp",EDGE,"E55"),sQuery(id+"F3.wireOp",EDGE,"E56")])],"isStart":true}),makeQuery(id+"F5.opExtrude","CAP_FACE",FACE,{"disambiguationData":[OSD([sQuery(id+"F3.wireOp",EDGE,"E61"),sQuery(id+"F3.wireOp",EDGE,"E62"),sQuery(id+"F3.wireOp",EDGE,"E63"),sQuery(id+"F3.wireOp",EDGE,"E64"),sQuery(id+"F3.wireOp",EDGE,"E65"),sQuery(id+"F3.wireOp",EDGE,"E66"),sQuery(id+"F3.wireOp",EDGE,"E67"),sQuery(id+"F3.wireOp",EDGE,"E68")])],"isStart":true}),makeQuery(id+"F5.opExtrude","CAP_FACE",FACE,{"disambiguationData":[OSD([sQuery(id+"F3.wireOp",EDGE,"E73"),sQuery(id+"F3.wireOp",EDGE,"E74"),sQuery(id+"F3.wireOp",EDGE,"E75"),subQ7,sQuery(id+"F3.wireOp",EDGE,"E77"),sQuery(id+"F3.wireOp",EDGE,"E78"),sQuery(id+"F3.wireOp",EDGE,"E79"),sQuery(id+"F3.wireOp",EDGE,"E80")])],"isStart":true}),makeQuery(id+"F5.opExtrude","SWEPT_FACE",FACE,{"disambiguationData":[OSD([subQ7])]}),makeQuery(id+"F5.opExtrude","CAP_FACE",FACE,{"disambiguationData":[OSD([subQ0]),OD(0.0)],"isStart":false}),makeQuery(id+"F5.opExtrude","CAP_FACE",FACE,{"disambiguationData":[OSD([subQ0]),OD(1.0)],"isStart":false}),makeQuery(id+"F5.opExtrude","CAP_FACE",FACE,{"disambiguationData":[OSD([subQ0]),OD(2.0)],"isStart":false}),makeQuery(id+"F5.opExtrude","CAP_FACE",FACE,{"disambiguationData":[OSD([subQ0]),OD(3.0)],"isStart":false}),makeQuery(id+"F5.opExtrude","CAP_FACE",FACE,{"disambiguationData":[OSD([subQ0]),OD(4.0)],"isStart":false})])],"derivedFrom":makeQuery(id+"F1.opExtrude","CAP_FACE",FACE,{"disambiguationData":[OSD([subQ4,sQuery(id+"F0.wireOp",EDGE,"E0.top"),subQ2,subQ5,sQuery(id+"F0.wireOp",EDGE,"E3.0.4.1"),sQuery(id+"F0.wireOp",EDGE,"E6"),subQ6,subQ1,subQ3,subQ0,sQuery(id+"F0.wireOp",EDGE,"E23.bottom"),sQuery(id+"F0.wireOp",EDGE,"E23.top"),sQuery(id+"F0.wireOp",EDGE,"E23.left"),sQuery(id+"F0.wireOp",EDGE,"E23.right")])],"isStart":false})});}
            var Q1;
            {var subQ0=sQuery(id+"F0.wireOp",EDGE,"E13.right");var subQ1=sQuery(id+"F0.wireOp",EDGE,"E0.left");var subQ2=sQuery(id+"F3.wireOp",EDGE,"f0gCdHVo-Gz2e-MZJZ-KHlR-wAMuaOjWp0eY");var subQ3=sQuery(id+"F0.wireOp",EDGE,"E22");var subQ4=sQuery(id+"F0.wireOp",EDGE,"E16");var subQ5=sQuery(id+"F0.wireOp",EDGE,"E0.top");var subQ6=sQuery(id+"F0.wireOp",EDGE,"E3.0.4.1");var subQ7=sQuery(id+"F0.wireOp",EDGE,"E6");Q1=makeQuery(id+"F5.boolean.opBoolean","SPLIT",FACE,{"disambiguationData":[TD([makeQuery(id+"F1.opExtrude","SWEPT_FACE",FACE,{"disambiguationData":[OSD([subQ5])]}),makeQuery(id+"F1.opExtrude","SWEPT_FACE",FACE,{"disambiguationData":[OSD([subQ1,subQ0])]}),makeQuery(id+"F1.opExtrude","SWEPT_FACE",FACE,{"disambiguationData":[OSD([subQ6])]}),makeQuery(id+"F1.opExtrude","SWEPT_FACE",FACE,{"disambiguationData":[OSD([subQ7])]}),makeQuery(id+"F1.opExtrude","SWEPT_FACE",FACE,{"disambiguationData":[OSD([subQ4]),TDD([makeQuery(id+"F0.imprint","IMPRINT",EDGE,{"disambiguationData":[TD([[makeQuery(id+"F0.imprint","INTERSECT",VERTEX,{"derivedFrom":[subQ5,subQ4]}),-1.0]])],"derivedFrom":subQ4})])]}),makeQuery(id+"F1.opExtrude","SWEPT_FACE",FACE,{"disambiguationData":[OSD([subQ3])]}),makeQuery(id+"F5.opExtrude","CAP_FACE",FACE,{"disambiguationData":[OSD([sQuery(id+"F3.wireOp",EDGE,"E26"),sQuery(id+"F3.wireOp",EDGE,"E27"),subQ2,sQuery(id+"F3.wireOp",EDGE,"E28"),sQuery(id+"F3.wireOp",EDGE,"E29"),sQuery(id+"F3.wireOp",EDGE,"E30"),sQuery(id+"F3.wireOp",EDGE,"E31"),sQuery(id+"F3.wireOp",EDGE,"E32")])],"isStart":true}),makeQuery(id+"F5.opExtrude","SWEPT_FACE",FACE,{"disambiguationData":[OSD([subQ2])]}),makeQuery(id+"F5.opExtrude","CAP_FACE",FACE,{"disambiguationData":[OSD([sQuery(id+"F3.wireOp",EDGE,"E37"),sQuery(id+"F3.wireOp",EDGE,"E38"),sQuery(id+"F3.wireOp",EDGE,"E39"),sQuery(id+"F3.wireOp",EDGE,"E40"),sQuery(id+"F3.wireOp",EDGE,"E41"),sQuery(id+"F3.wireOp",EDGE,"E42"),sQuery(id+"F3.wireOp",EDGE,"E43"),sQuery(id+"F3.wireOp",EDGE,"E44")])],"isStart":true}),makeQuery(id+"F5.opExtrude","CAP_FACE",FACE,{"disambiguationData":[OSD([sQuery(id+"F3.wireOp",EDGE,"E49"),sQuery(id+"F3.wireOp",EDGE,"E50"),sQuery(id+"F3.wireOp",EDGE,"E51"),sQuery(id+"F3.wireOp",EDGE,"E52"),sQuery(id+"F3.wireOp",EDGE,"E53"),sQuery(id+"F3.wireOp",EDGE,"E54"),sQuery(id+"F3.wireOp",EDGE,"E55"),sQuery(id+"F3.wireOp",EDGE,"E56")])],"isStart":true}),makeQuery(id+"F5.opExtrude","CAP_FACE",FACE,{"disambiguationData":[OSD([sQuery(id+"F3.wireOp",EDGE,"E61"),sQuery(id+"F3.wireOp",EDGE,"E62"),sQuery(id+"F3.wireOp",EDGE,"E63"),sQuery(id+"F3.wireOp",EDGE,"E64"),sQuery(id+"F3.wireOp",EDGE,"E65"),sQuery(id+"F3.wireOp",EDGE,"E66"),sQuery(id+"F3.wireOp",EDGE,"E67"),sQuery(id+"F3.wireOp",EDGE,"E68")])],"isStart":true}),makeQuery(id+"F5.opExtrude","CAP_FACE",FACE,{"disambiguationData":[OSD([sQuery(id+"F3.wireOp",EDGE,"E73"),sQuery(id+"F3.wireOp",EDGE,"E74"),sQuery(id+"F3.wireOp",EDGE,"E75"),sQuery(id+"F3.wireOp",EDGE,"E76"),sQuery(id+"F3.wireOp",EDGE,"E77"),sQuery(id+"F3.wireOp",EDGE,"E78"),sQuery(id+"F3.wireOp",EDGE,"E79"),sQuery(id+"F3.wireOp",EDGE,"E80")])],"isStart":true}),makeQuery(id+"F5.opExtrude","CAP_FACE",FACE,{"disambiguationData":[OSD([subQ3]),OD(0.0)],"isStart":false}),makeQuery(id+"F5.opExtrude","CAP_FACE",FACE,{"disambiguationData":[OSD([subQ3]),OD(1.0)],"isStart":false}),makeQuery(id+"F5.opExtrude","CAP_FACE",FACE,{"disambiguationData":[OSD([subQ3]),OD(2.0)],"isStart":false}),makeQuery(id+"F5.opExtrude","CAP_FACE",FACE,{"disambiguationData":[OSD([subQ3]),OD(3.0)],"isStart":false}),makeQuery(id+"F5.opExtrude","CAP_FACE",FACE,{"disambiguationData":[OSD([subQ3]),OD(4.0)],"isStart":false})])],"derivedFrom":makeQuery(id+"F1.opExtrude","CAP_FACE",FACE,{"disambiguationData":[OSD([sQuery(id+"F0.wireOp",EDGE,"E0.bottom"),subQ5,subQ1,sQuery(id+"F0.wireOp",EDGE,"E2.2.1.1"),subQ6,subQ7,sQuery(id+"F0.wireOp",EDGE,"E7.MirrorC"),subQ0,subQ4,subQ3,sQuery(id+"F0.wireOp",EDGE,"E23.bottom"),sQuery(id+"F0.wireOp",EDGE,"E23.top"),sQuery(id+"F0.wireOp",EDGE,"E23.left"),sQuery(id+"F0.wireOp",EDGE,"E23.right")])],"isStart":false})});}
            var Q2;
            Q2=makeQuery(id+"F5.opExtrude","SWEPT_FACE",FACE,{"disambiguationData":[OSD([sQuery(id+"F3.wireOp",EDGE,"E77")])]});
            extrude(context, id + "F9", {"entities" : qUnion([Q0, Q1]), "operationType" : NewBodyOperationType.ADD, "depth" : 1.5 * mm, "endBoundEntityFace" : qUnion([Q2]), "offsetDistance" : 25.4 * mm});
        }
        {
            var Q0;
            Q0=makeQuery(id+"F8.imprint","IMPRINT",FACE,{"disambiguationData":[TD([[makeQuery(id+"F8.imprint","IMPRINT",EDGE,{"derivedFrom":sQuery(id+"F8.wireOp",EDGE,"E87.0")}),-1.0]])]});
            var Q1;
            Q1=makeQuery(id+"F8.imprint","IMPRINT",FACE,{"disambiguationData":[TD([[makeQuery(id+"F8.imprint","IMPRINT",EDGE,{"derivedFrom":sQuery(id+"F8.wireOp",EDGE,"E88.0")}),-1.0]])]});
            extrude(context, id + "F10", {"entities" : qUnion([Q0, Q1]), "operationType" : NewBodyOperationType.REMOVE, "endBound" : BoundingType.THROUGH_ALL, "depth" : 25.4 * mm, "offsetDistance" : 25.4 * mm});
        }
    });
